# Revit family: NAU_Naughtone_Tbls_Knot1
name_source: partatom
category: Furniture
revit_build: Autodesk Revit 2015 (Build: 20140903_1530(x64)
units: mm (PartAtom-declared; Revit-internal decimal feet)

## types (2) — shared parameters
Assembly Code = E2020200
AssetType = Movable
BIMObjectName = NAU_Naughtone_Tables_Knot
Category = Pr_40_50_21 Desks, tables and worktops
Color = Various
DurationUnit = year
IfcExportAs = IfcFurnishingElementType
IfcExportType = TABLE
Keynote = Pr_40_50_21
MainColor = Various
ManufacturerAddressUK = Knaresborough Tech Park, Manse Lane, Knaresborough, HG5 8LF
ManufacturerName = Naughtone
ManufacturerURL = www.naughtone.com
Material = Mild Steel, Veneered MDF, MFMDF, Forbo Lino
NBSDescription = Tables
NBSReference = 45-35-86/327
Name = Tables_Knot_Naughtone
NominalHeight = 650 mm  [stored 2.13255 ft]
URL = www.naughtone.com
Uniclass2015Description = Desks, tables and worktops
Uniclass2015Reference = Pr_40_50_21
Uniclass2015Version = Products v1.6
Version = 1
WarrantyDescription = Request warranty information from naughtone
WarrantyDurationLabor = 5
WarrantyDurationParts = 5
WarrantyDurationUnit = year
zero-valued in all types: NumberOfChairs, WorksurfaceArea

## per-type parameters (varying)
| type | Description | KNO55D | ModelReference | NominalLength | NominalWidth | Shape | Size | SustainabilityPerformance |
| KNO50X40 | Knot Rectangular Side Table | No | Knot Rectangular Side Table | 500 mm  [stored 1.64042 ft] | 400 mm  [stored 1.31234 ft] | Rectangular | 500x400x650mm | FSC certified. FISP certified. ISO 14001 certified |
| KNO550D | Knot 550 Circular Side Table | Yes | Knot 550 Circular Side Table | 550 mm | 550 mm | Circular | 525x425x650mm | FSC certified. FISP certified. ISO 14001. CARB |

note: column(s) folded — value = type name in every type: Model, ModelNumber

note: [stored X ft] marks values corroborated as IEEE doubles in the binary element streams (Revit-internal decimal feet)

## geometry (parser evidence)
native form markers: Sweep x2
no freeform markers — native parametric forms only
